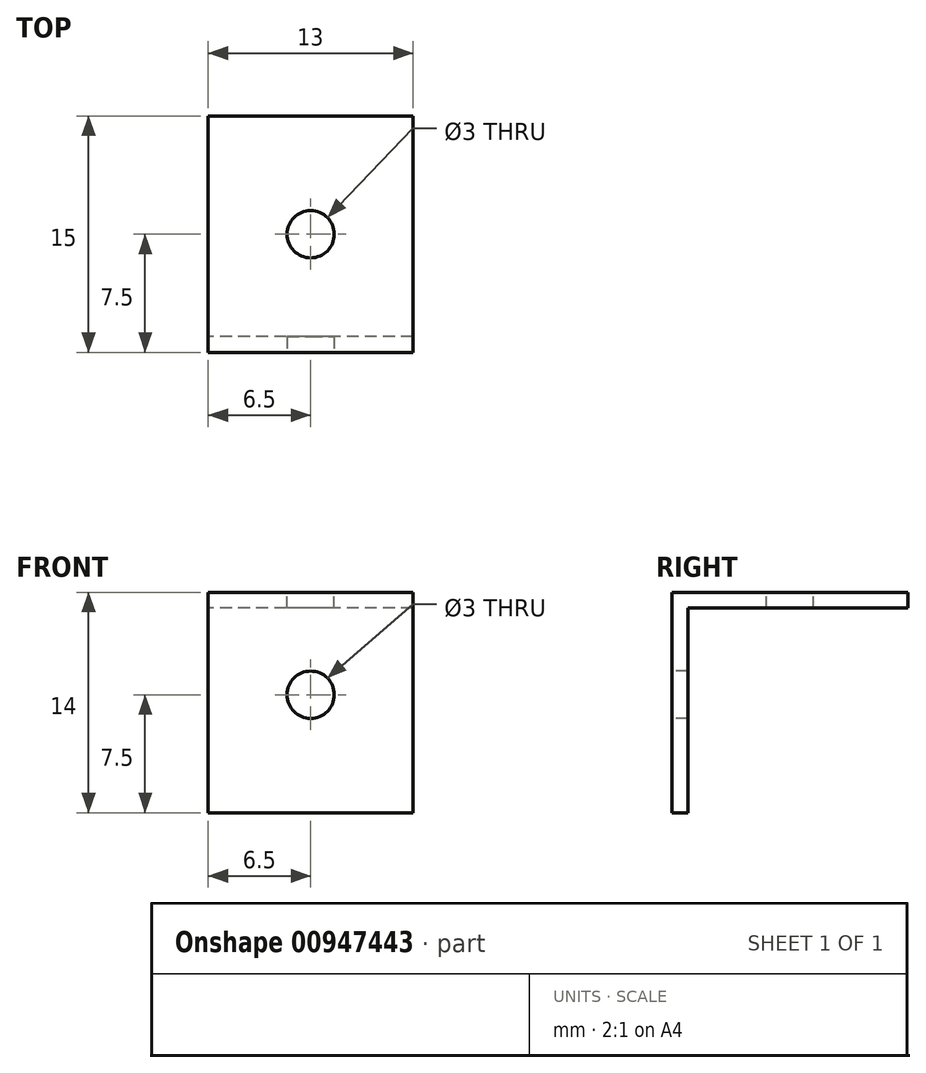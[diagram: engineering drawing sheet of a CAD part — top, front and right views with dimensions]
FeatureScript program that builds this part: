
annotation { "Feature Type Name" : "Feature", "Feature Type Description" : "" }
export const myFeature = defineFeature(function(context is Context, id is Id, definition is map)
    precondition{}
    {
        {
            var Q0;
            Q0=qCreatedBy(makeId("Right.planeOp"),FACE);
            var sketch = newSketch(context, id + "F0", { "sketchPlane" : qUnion([Q0])});
            skLineSegment(sketch, "E0.bottom", {"start": v(-6.5, -7) * mm, "end": v(-7.5, -7) * mm});
            skLineSegment(sketch, "E0.top", {"start": v(7.5, 7) * mm, "end": v(-7.5, 7) * mm});
            skLineSegment(sketch, "E0.left", {"start": v(7.5, 6) * mm, "end": v(7.5, 7) * mm});
            skLineSegment(sketch, "E0.right", {"start": v(-7.5, -7) * mm, "end": v(-7.5, 7) * mm});
            skPoint(sketch, "E0.middle", {"position": v(0, 0) * mm});
            skLineSegment(sketch, "E1", {"start": v(-6.5, -7) * mm, "end": v(-6.5, 6) * mm});
            skLineSegment(sketch, "E2", {"start": v(-6.5, 6) * mm, "end": v(7.5, 6) * mm});
            skPoint(sketch, "E3.orphan", {"position": v(7.5, -7) * mm});
            skSolve(sketch);
        }
        {
            var Q0;
            Q0=makeQuery(id+"F0.imprint","IMPRINT",FACE,{"disambiguationData":[TD([[makeQuery(id+"F0.imprint","IMPRINT",EDGE,{"derivedFrom":sQuery(id+"F0.wireOp",EDGE,"E0.bottom")}),-1.0]])]});
            extrude(context, id + "F1", {"entities" : qUnion([Q0]), "depth" : 13 * mm, "offsetDistance" : 25 * mm});
        }
        {
            var Q0;
            Q0=makeQuery(id+"F1.opExtrude","SWEPT_FACE",FACE,{"disambiguationData":[OSD([sQuery(id+"F0.wireOp",EDGE,"E0.top")])]});
            var sketch = newSketch(context, id + "F2", { "sketchPlane" : qUnion([Q0])});
            skCircle(sketch, "E4", {"center": v(6.5, 0) * mm, "radius": 1.5 * mm});
            skPoint(sketch, "E4.centerSnap0", {"position": v(6.5, 7.5) * mm});
            skSolve(sketch);
        }
        {
            var Q0;
            Q0=makeQuery(id+"F2.imprint","IMPRINT",FACE,{"disambiguationData":[TD([[makeQuery(id+"F2.imprint","IMPRINT",EDGE,{"derivedFrom":sQuery(id+"F2.wireOp",EDGE,"E4")}),1.0]])]});
            extrude(context, id + "F3", {"entities" : qUnion([Q0]), "operationType" : NewBodyOperationType.REMOVE, "endBound" : BoundingType.UP_TO_NEXT, "oppositeDirection" : true, "depth" : 25 * mm, "offsetDistance" : 25 * mm});
        }
        {
            var Q0;
            Q0=makeQuery(id+"F1.opExtrude","SWEPT_FACE",FACE,{"disambiguationData":[OSD([sQuery(id+"F0.wireOp",EDGE,"E0.right")])]});
            var sketch = newSketch(context, id + "F4", { "sketchPlane" : qUnion([Q0])});
            skCircle(sketch, "E5", {"center": v(6.5, 0.5) * mm, "radius": 1.5 * mm});
            skPoint(sketch, "E5.centerSnap0", {"position": v(6.5, 7) * mm});
            skSolve(sketch);
        }
        {
            var Q0;
            Q0=makeQuery(id+"F4.imprint","IMPRINT",FACE,{"disambiguationData":[TD([[makeQuery(id+"F4.imprint","IMPRINT",EDGE,{"derivedFrom":sQuery(id+"F4.wireOp",EDGE,"E5")}),1.0]])]});
            extrude(context, id + "F5", {"entities" : qUnion([Q0]), "operationType" : NewBodyOperationType.REMOVE, "endBound" : BoundingType.UP_TO_NEXT, "oppositeDirection" : true, "depth" : 25 * mm, "offsetDistance" : 25 * mm});
        }
    });
